# Revit family: PRD_FrankeWS_Splshbcks_AnimaSplashback_SB400,450,500,600
name_source: partatom
category: Furniture
revit_build: Autodesk Revit 2018 (Build: 20190510_1515(x64)
units: mm (PartAtom-declared; Revit-internal decimal feet)

## family parameters
Cut with Voids When Loaded = No
Host = Face
OmniClass Number = 23.45.00.00
OmniClass Title = Sanitary, Laundry, and Cleaning Equipment
Room Calculation Point = No
Shared = No

## types (4) — shared parameters
AssetType = Fixed
Category = Pr_40_20_76_83, Splashbacks
Color = Stainless steel
Default Elevation = 850 mm  [stored 2.78871 ft]
DurationUnit = year
Edges = Square
Finish = Satin finished
FixingHoles = Pre-drilled
IfcExportAs = IfcFurnitureType
IfcExportType = NOTDEFINED
MainColor = Stainless steel
Manufacturer = KWC Group AG
ManufacturerName = KWC Group AG
ManufacturerURL = www.kwc.com
Material = Stainless steel 1.4301
NBSDescription = Splashbacks
NBSReference = 45-35-15/464
ProductInformation = https://pim.kwc.com
Shape = Rectangular
SplashbackMaterial = PRD_AR_StainlessSteel_SatinFinished
Style = Splashback
URL = www.kwc.com
Uniclass2015Code = Pr_40_20_76_83
Uniclass2015Title = Splashbacks
Version = 1
WarrantyDurationUnit = year
zero-valued in all types: NominalWidth

## per-type parameters (varying)
| type | BIMObjectName | Description | Features | GrossWeight | ModelNumber | Name | NetWeight | NominalDepth | NominalHeight | NominalLength | SB400,500,600 | SB450 | Size | Uniclass2015Version |
| SB400 | PRD_AR_Splashbacks_AnimaSplashback_SB400 | Splash back for wall mounting, stainless steel, surface satin finished, material thickness 1 mm, incl. stainless steel screws and dowels. Suitable for washbasins WT400A and WT400C, length 400 mm | stainless steel, 1 mm, satin finished, wall mounting, 400x200x1 mm (WxHxD) | 0.80 kg | 2000100065 | Anima splashback SB400 | 0.60 kg | 1 mm  [stored 0.00328084 ft] | 200 mm  [stored 0.656168 ft] | 400 mm  [stored 1.31234 ft] | Yes | No | 400 x 200 x 1 mm | Products v1.5 |
| SB500 | PRD_AR_Splashbacks_AnimaSplashback_SB500 | Splash back for wall mounting, stainless steel, surface satin finished, material thickness 1 mm, inclusive stainless steel screws and dowels. Suitable for washbasins WT500A and WT500C, length 500 mm | stainless steel, 1 mm, satin finished, wall mounting, 500x200x1 mm (WxHxD) | 0.90 kg | 2000100066 | Anima splashback SB500 | 0.70 kg | 1 mm  [stored 0.00328084 ft] | 200 mm  [stored 0.656168 ft] | 500 mm  [stored 1.64042 ft] | Yes | No | 500 x 200 x 1 mm | Products v1.10 |
| SB600 | PRD_AR_Splashbacks_AnimaSplashback_SB600 | Splash back for wall mounting, stainless steel, surface satin finished, material thickness 1 mm, incl. stainless steel screws and dowels. Suitable for washbasins WT600A and WT600C, lenght 600 mm | stainless steel, 1 mm, satin finished, wall mounting, 600x250x1 mm (WxHxD) | 1.30 kg | 2000100067 | Anima splashback SB600 | 1.00 kg | 1 mm  [stored 0.00328084 ft] | 250 mm  [stored 0.82021 ft] | 600 mm | Yes | No | 600 x 250 x 1 mm | Products v1.10 |
| SB450 | PRD_AR_Splashbacks_AnimaSplashback_SB450 | Splash back for wall mounting, stainless steel, surface satin finished, material thickness 0.9 mm, includes stainless steel screws and dowels. Suitable to WT450, LP20 and LP21, length 450 mm | stainless steel, 0.90 mm, satin finished, wall mounting, 450x210x12 mm (WxHxD) | 1.53 kg | 2000100338 | Anima splashback SB450 | 1.03 kg | 12 mm  [stored 0.0393701 ft] | 210 mm  [stored 0.688976 ft] | 450 mm  [stored 1.47638 ft] | No | Yes | 450 x 210 x 12 mm | Products v1.10 |

note: column(s) folded — value = type name in every type: Model, ModelReference

note: [stored X ft] marks values corroborated as IEEE doubles in the binary element streams (Revit-internal decimal feet)

## geometry (parser evidence)
native form markers: Sweep x5
no freeform markers — native parametric forms only
